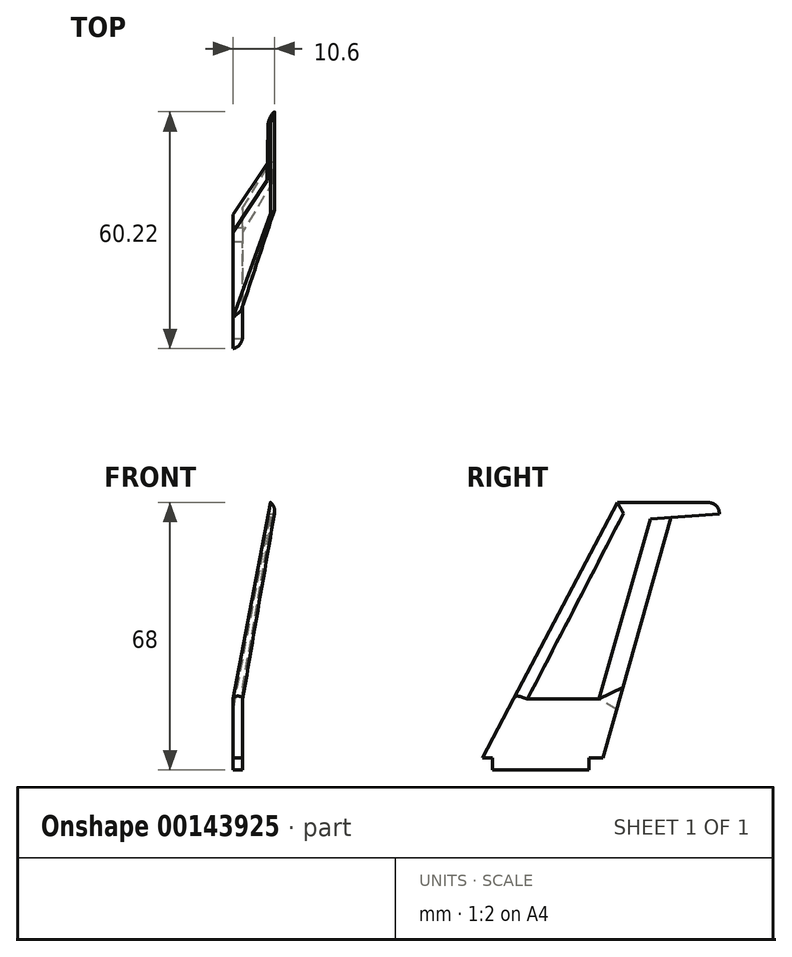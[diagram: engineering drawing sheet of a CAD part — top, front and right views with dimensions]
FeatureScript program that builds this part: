
annotation { "Feature Type Name" : "Feature", "Feature Type Description" : "" }
export const myFeature = defineFeature(function(context is Context, id is Id, definition is map)
    precondition{}
    {
        {
            var Q0;
            Q0=qCreatedBy(makeId("Top.planeOp"),FACE);
            var sketch = newSketch(context, id + "F0", { "sketchPlane" : qUnion([Q0])});
            skLineSegment(sketch, "E0", {"start": v(0, 0) * mm, "end": v(-2.5, 0) * mm});
            skLineSegment(sketch, "E1", {"start": v(-2.5, 0) * mm, "end": v(-2.5, 24.5) * mm});
            skLineSegment(sketch, "E2", {"start": v(-2.5, 24.5) * mm, "end": v(0, 24.5) * mm});
            skLineSegment(sketch, "E3", {"start": v(0, 24.5) * mm, "end": v(0, 0) * mm});
            skSolve(sketch);
        }
        {
            var Q0;
            Q0=qSketchRegion(id+"F0",true);
            extrude(context, id + "F1", {"entities" : qUnion([Q0]), "depth" : 3 * mm});
        }
        {
            var Q0;
            Q0=makeQuery(id+"F1.opExtrude","SWEPT_FACE",FACE,{"disambiguationData":[OSD([sQuery(id+"F0.wireOp",EDGE,"E0")])]});
            var sketch = newSketch(context, id + "F2", { "sketchPlane" : qUnion([Q0])});
            skLineSegment(sketch, "E4", {"start": v(0, 3) * mm, "end": v(0, 18) * mm});
            skLineSegment(sketch, "E5", {"start": v(0, 3) * mm, "end": v(-2.5, 3) * mm});
            skLineSegment(sketch, "E6", {"start": v(-2.5, 3) * mm, "end": v(-2.5, 18) * mm});
            skLineSegment(sketch, "E7", {"start": v(-2.5, 18) * mm, "end": v(0, 18) * mm});
            skLineSegment(sketch, "E8", {"start": v(0, 18) * mm, "end": v(-9.54, 68) * mm});
            skLineSegment(sketch, "E9", {"start": v(-2.5, 18) * mm, "end": v(-11.04, 68) * mm});
            skLineSegment(sketch, "E10.trimOffspring", {"start": v(-9.54, 68) * mm, "end": v(-11.04, 68) * mm});
            skSolve(sketch);
        }
        {
            var Q0;
            Q0=qSketchRegion(id+"F2",true);
            extrude(context, id + "F3", {"entities" : qUnion([Q0]), "operationType" : NewBodyOperationType.ADD, "oppositeDirection" : true, "depth" : 120 * mm, "symmetric" : true});
        }
        {
            var Q0;
            Q0=qCreatedBy(makeId("Right.planeOp"),FACE);
            var sketch = newSketch(context, id + "F4", { "sketchPlane" : qUnion([Q0])});
            skLineSegment(sketch, "E11", {"start": v(-2.64, 3) * mm, "end": v(31.64, 68) * mm});
            skLineSegment(sketch, "E12", {"start": v(31.64, 68) * mm, "end": v(57.58, 68) * mm});
            skLineSegment(sketch, "E13", {"start": v(57.58, 65) * mm, "end": v(45.33, 64.16) * mm});
            skLineSegment(sketch, "E14", {"start": v(45.33, 64.16) * mm, "end": v(28, 3) * mm});
            skLineSegment(sketch, "E15", {"start": v(57.58, 68) * mm, "end": v(57.58, 65) * mm});
            skLineSegment(sketch, "E16", {"start": v(28, 3) * mm, "end": v(67.76, 3) * mm});
            skLineSegment(sketch, "E17", {"start": v(67.76, 3) * mm, "end": v(67.76, 72.01) * mm});
            skLineSegment(sketch, "E18", {"start": v(67.76, 72.01) * mm, "end": v(0, 72.01) * mm});
            skLineSegment(sketch, "E19", {"start": v(-2.64, 3) * mm, "end": v(-65.16, 3) * mm});
            skLineSegment(sketch, "E20", {"start": v(-65.16, 3) * mm, "end": v(-65.16, 72.01) * mm});
            skLineSegment(sketch, "E21", {"start": v(-65.16, 72.01) * mm, "end": v(0, 72.01) * mm});
            skPoint(sketch, "E22.orphan", {"position": v(0, 3) * mm});
            skSolve(sketch);
        }
        {
            var Q0;
            Q0=qSketchRegion(id+"F4",true);
            extrude(context, id + "F5", {"entities" : qUnion([Q0]), "operationType" : NewBodyOperationType.REMOVE, "oppositeDirection" : true, "depth" : 25 * mm});
        }
        {
            var Q0;
            Q0=makeQuery(id+"F5.boolean.opBoolean","INTERSECT",EDGE,{"derivedFrom":[makeQuery(id+"F3.opExtrude","SWEPT_FACE",FACE,{"disambiguationData":[OSD([sQuery(id+"F2.wireOp",EDGE,"E9")])]}),makeQuery(id+"F5.opExtrude","SWEPT_FACE",FACE,{"disambiguationData":[OSD([sQuery(id+"F4.wireOp",EDGE,"E14")])]})]});
            var Q1;
            Q1=makeQuery(id+"F5.boolean.opBoolean","INTERSECT",EDGE,{"derivedFrom":[makeQuery(id+"F3.opExtrude","SWEPT_FACE",FACE,{"disambiguationData":[OSD([sQuery(id+"F2.wireOp",EDGE,"E8")])]}),makeQuery(id+"F5.opExtrude","SWEPT_FACE",FACE,{"disambiguationData":[OSD([sQuery(id+"F4.wireOp",EDGE,"E14")])]})]});
            chamfer(context, id + "F6", {"entities" : qUnion([Q0, Q1]), "chamferType" : ChamferType.TWO_OFFSETS, "width1" : 5 * mm, "oppositeDirection" : false, "width2" : .5 * mm, "tangentPropagation" : true});
        }
        {
            var Q0;
            Q0=makeQuery(id+"F5.boolean.opBoolean","INTERSECT",EDGE,{"derivedFrom":[makeQuery(id+"F3.opExtrude","SWEPT_FACE",FACE,{"disambiguationData":[OSD([sQuery(id+"F2.wireOp",EDGE,"E9")])]}),makeQuery(id+"F5.opExtrude","SWEPT_FACE",FACE,{"disambiguationData":[OSD([sQuery(id+"F4.wireOp",EDGE,"E11")])]})]});
            var Q1;
            Q1=makeQuery(id+"F5.boolean.opBoolean","INTERSECT",EDGE,{"derivedFrom":[makeQuery(id+"F3.boolean.opBoolean","MERGE",FACE,{"derivedFrom":[makeQuery(id+"F1.opExtrude","SWEPT_FACE",FACE,{"disambiguationData":[OSD([sQuery(id+"F0.wireOp",EDGE,"E1")])]}),makeQuery(id+"F3.opExtrude","SWEPT_FACE",FACE,{"disambiguationData":[OSD([sQuery(id+"F2.wireOp",EDGE,"E6")])]})]}),makeQuery(id+"F5.opExtrude","SWEPT_FACE",FACE,{"disambiguationData":[OSD([sQuery(id+"F4.wireOp",EDGE,"E11")])]})]});
            var Q2;
            Q2=makeQuery(id+"F3.opExtrude","SWEPT_EDGE",EDGE,{"disambiguationData":[OSD([sQuery(id+"F2.wireOp",EDGE,"E9"),sQuery(id+"F2.wireOp",EDGE,"E10.trimOffspring")])]});
            fillet(context, id + "F7", {"entities" : qUnion([Q0, Q1, Q2]), "radius" : 3 * mm, "tangentPropagation" : true, "allowEdgeOverflow" : false});
        }
        {
            var Q0;
            Q0=makeQuery(id+"F7.opFillet","BLEND_EDGE",EDGE,{"blendedFrom":[makeQuery(id+"F3.opExtrude","SWEPT_EDGE",EDGE,{"disambiguationData":[OSD([sQuery(id+"F2.wireOp",EDGE,"E8"),sQuery(id+"F2.wireOp",EDGE,"E10.trimOffspring")])]}),makeQuery(id+"F5.boolean.opBoolean","COPY",FACE,{"derivedFrom":makeQuery(id+"F5.opExtrude","SWEPT_FACE",FACE,{"disambiguationData":[OSD([sQuery(id+"F4.wireOp",EDGE,"E15")])]})})],"blendedInto":[makeQuery(id+"F5.boolean.opBoolean","COPY",FACE,{"derivedFrom":makeQuery(id+"F5.opExtrude","SWEPT_FACE",FACE,{"disambiguationData":[OSD([sQuery(id+"F4.wireOp",EDGE,"E15")])]})})]});
            var Q1;
            Q1=makeQuery(id+"F5.boolean.opBoolean","INTERSECT",EDGE,{"derivedFrom":[makeQuery(id+"F3.opExtrude","SWEPT_FACE",FACE,{"disambiguationData":[OSD([sQuery(id+"F2.wireOp",EDGE,"E8")])]}),makeQuery(id+"F5.opExtrude","SWEPT_FACE",FACE,{"disambiguationData":[OSD([sQuery(id+"F4.wireOp",EDGE,"E15")])]})]});
            fillet(context, id + "F8", {"entities" : qUnion([Q0, Q1]), "radius" : 5 * mm, "tangentPropagation" : true, "allowEdgeOverflow" : false});
        }
        {
            var Q0;
            Q0=makeQuery(id+"F1.opExtrude","SWEPT_BODY",BODY,{"disambiguationData":[OSD([sQuery(id+"F0.wireOp",EDGE,"E0"),sQuery(id+"F0.wireOp",EDGE,"E1"),sQuery(id+"F0.wireOp",EDGE,"E2"),sQuery(id+"F0.wireOp",EDGE,"E3")])]});
            var Q1;
            Q1=qCreatedBy(makeId("Right.planeOp"),FACE);
            mirror(context, id + "F9", {"entities" : qUnion([Q0]), "mirrorPlane" : qUnion([Q1])});
        }
        {
            var Q0;
            Q0=makeQuery(id+"F1.opExtrude","SWEPT_BODY",BODY,{"disambiguationData":[OSD([sQuery(id+"F0.wireOp",EDGE,"E0"),sQuery(id+"F0.wireOp",EDGE,"E1"),sQuery(id+"F0.wireOp",EDGE,"E2"),sQuery(id+"F0.wireOp",EDGE,"E3")])]});
            deleteBodies(context, id + "F10", {"entities" : qUnion([Q0])});
        }
    });
